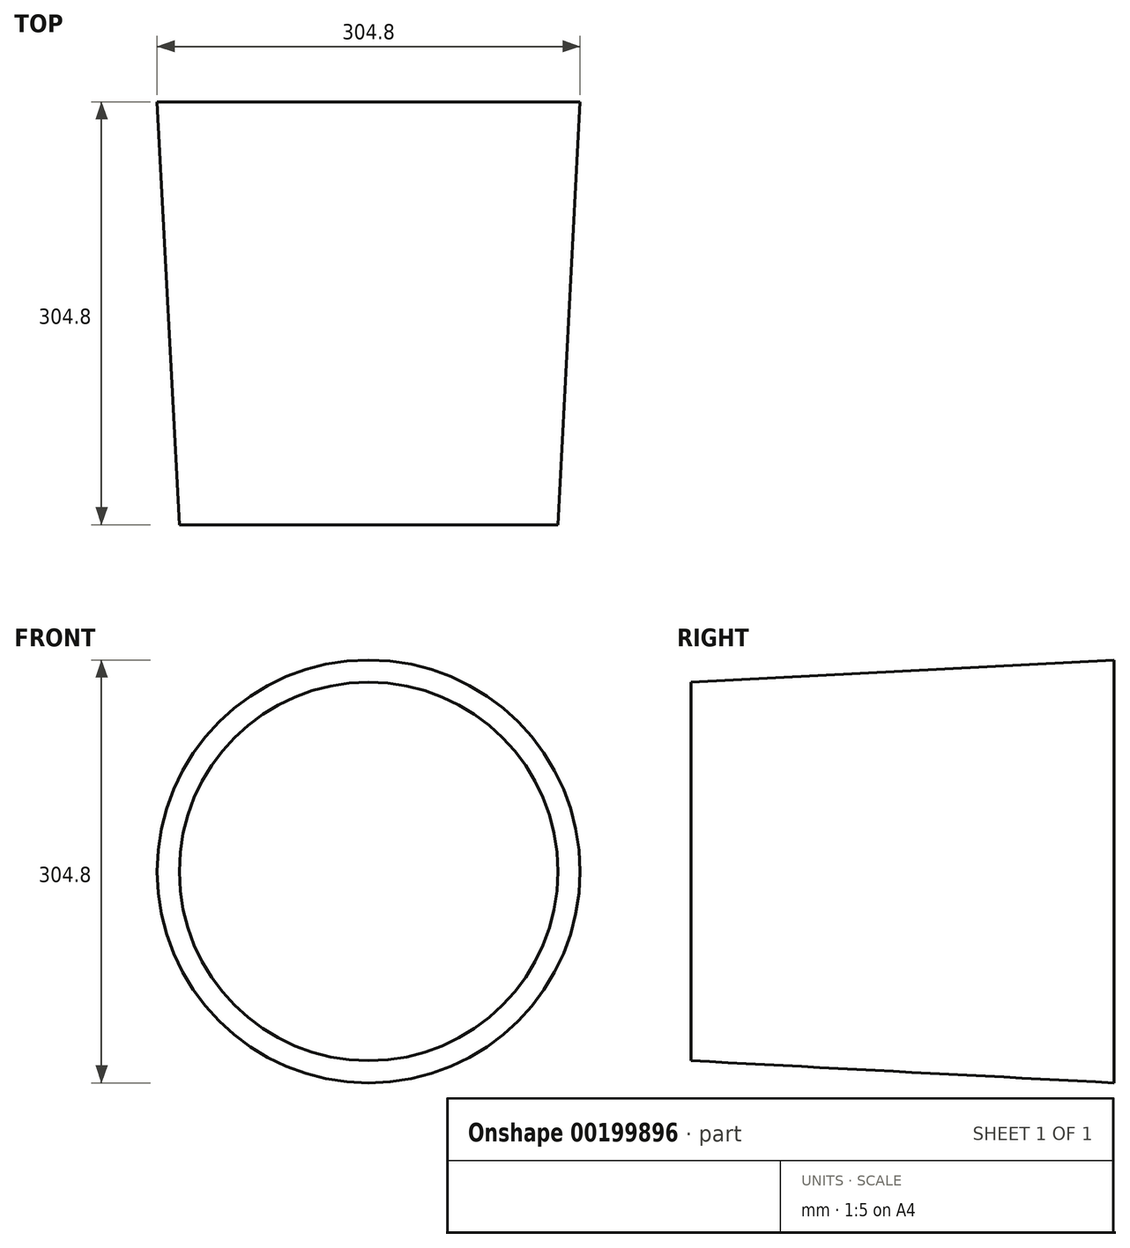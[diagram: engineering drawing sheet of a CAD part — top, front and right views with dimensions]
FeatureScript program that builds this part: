
annotation { "Feature Type Name" : "Feature", "Feature Type Description" : "" }
export const myFeature = defineFeature(function(context is Context, id is Id, definition is map)
    precondition{}
    {
        {
            var Q0;
            Q0=qCreatedBy(makeId("Front.planeOp"),FACE);
            var sketch = newSketch(context, id + "F0", { "sketchPlane" : qUnion([Q0])});
            skCircle(sketch, "E0", {"center": v(0, 0) * mm, "radius": 152.4 * mm});
            skSolve(sketch);
        }
        {
            var Q0;
            Q0 = qSketchRegion(id + "F0", true);
            extrude(context, id + "F1", {"entities" : qUnion([Q0]), "depth" : 304.8 * mm, "hasDraft" : true, "draftAngle" : 3 * degree, "draftPullDirection" : true});
        }
    });
